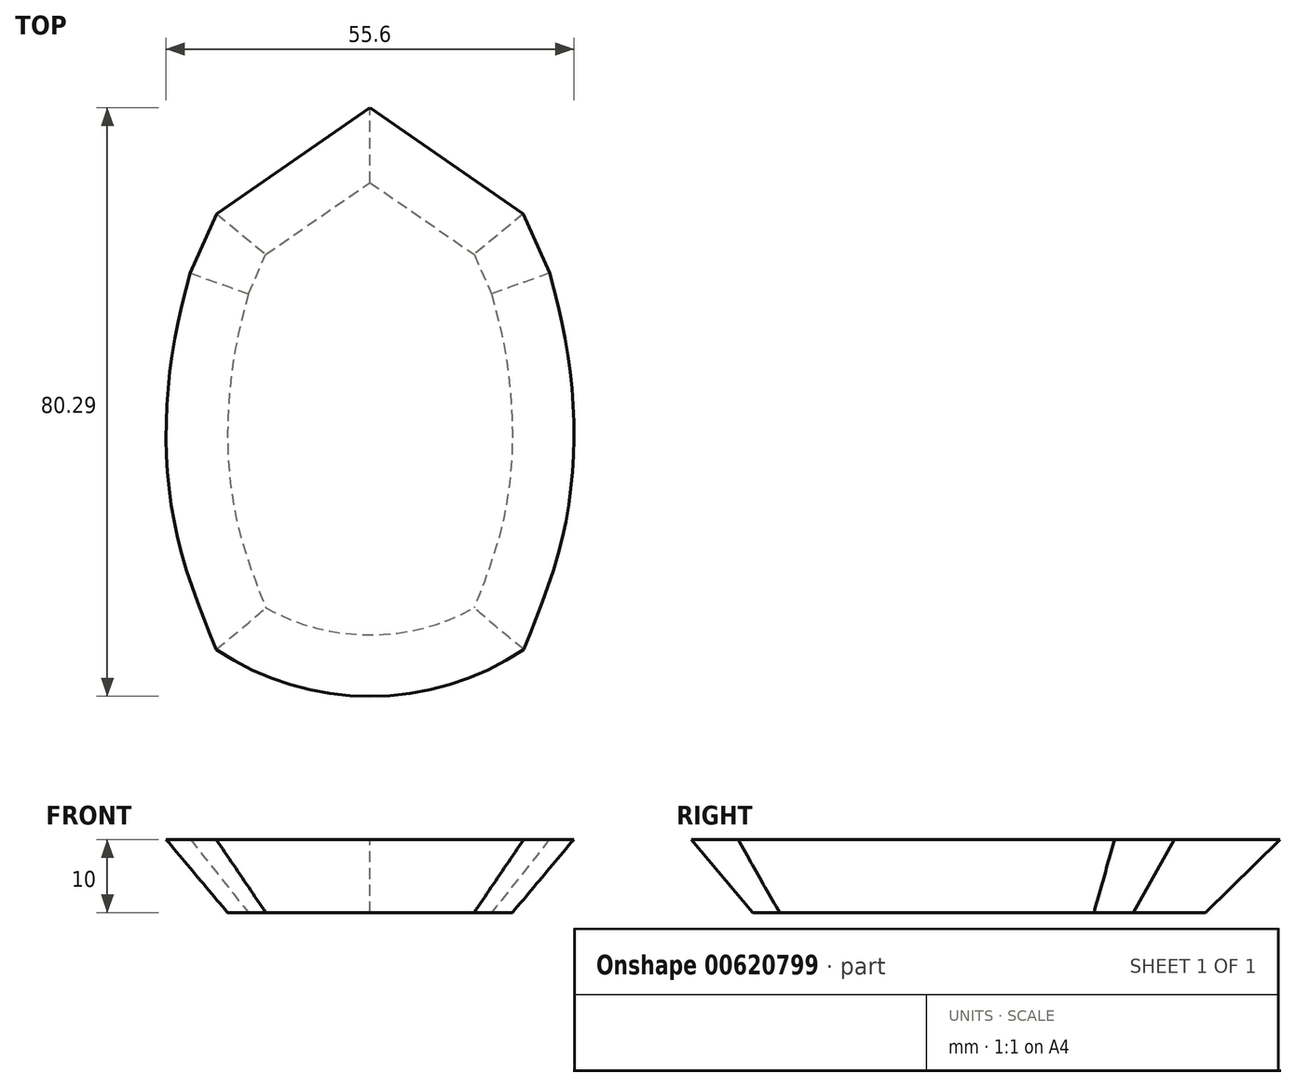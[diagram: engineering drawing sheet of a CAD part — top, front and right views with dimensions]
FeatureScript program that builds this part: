
annotation { "Feature Type Name" : "Feature", "Feature Type Description" : "" }
export const myFeature = defineFeature(function(context is Context, id is Id, definition is map)
    precondition{}
    {
        {
            var Q0;
            Q0=qCreatedBy(makeId("Top.planeOp"), FACE);
            var sketch = newSketch(context, id + "F0", { "sketchPlane" : qUnion([Q0])});
            skLineSegment(sketch, "E0", {"start": v(0, 75.27) * mm, "end": v(0, -80.16) * mm, "construction": true});
            skLineSegment(sketch, "E1", {"start": v(0, 75.27) * mm, "end": v(-14.2, 65.46) * mm});
            skLineSegment(sketch, "E2", {"start": v(-14.2, 65.46) * mm, "end": v(-16.57, 60.09) * mm});
            skFitSpline(sketch, "E3", {"points": [v(-16.57, 60.09) * mm, v(-18.3, 52.82) * mm, v(-19.41, 40.89) * mm, v(-17.91, 28.09) * mm, v(-14.2, 17.26) * mm], "startDerivative": vector(-8.9, -32.72) * mm, "endDerivative": vector(16.18, -40.98) * mm});
            skLineSegment(sketch, "E4.MirrorCS", {"start": v(0, 75.27) * mm, "end": v(14.2, 65.46) * mm});
            skLineSegment(sketch, "E5.MirrorCS", {"start": v(14.2, 65.46) * mm, "end": v(16.57, 60.09) * mm});
            skFitSpline(sketch, "E6.MirrorCS", {"points": [v(16.57, 60.09) * mm, v(18.3, 52.82) * mm, v(19.41, 40.89) * mm, v(17.91, 28.09) * mm, v(14.2, 17.26) * mm], "startDerivative": vector(8.9, -32.72) * mm, "endDerivative": vector(-16.18, -40.98) * mm});
            skArc(sketch, "E7", {"start": v(-14.2, 17.26) * mm, "mid": v(0, 13.57) * mm, "end": v(14.2, 17.26) * mm});
            skSolve(sketch);
        }
        {
            var Q0;
            Q0 = qSketchRegion(id + "F0", true);
            extrude(context, id + "F1", {"entities" : qUnion([Q0]), "surfaceOperationType" : NewSurfaceOperationType.ADD, "depth" : 10 * mm, "offsetDistance" : 25 * mm, "hasDraft" : true, "draftAngle" : 40 * degree});
        }
    });
